# Revit family: BuzziZepp
name_source: partatom
category: Generic Models
revit_build: Autodesk Revit 2018 (Build: 20180329_1100(x64)
units: mm (PartAtom-declared; Revit-internal decimal feet)

## family parameters
Always vertical = Yes
Can host rebar = No
Cut with Voids When Loaded = No
Host = Ceiling
Part Type = Normal
Room Calculation Point = No
Round Connector Dimension = Use Diameter
Shared = No

## types (4) — shared parameters
BuzzZepp Material = <By Category>
Cable Material = <By Category>
Fixture Housing Material = <By Category>
Lens Material = <By Category>

## type names
- BuzziZepp Small
- BuzziZepp Medium
- BuzziZepp Small LED
- BuzziZepp Medium LED
type visibility flags (boolean, named after types; folded from table):
- BuzziZepp Small: Yes: BuzziZepp Small
- BuzziZepp Medium: Yes: BuzziZepp Medium
- BuzziZepp Small LED: Yes: BuzziZepp Small, BuzziZepp Small Light Fixture
- BuzziZepp Medium LED: Yes: BuzziZepp Medium, BuzziZepp Medium Light Fixture

## geometry (parser evidence)
native form markers: Sweep x15
no freeform markers — native parametric forms only
